# Revit family: Shower-Shower_Trim-KOHLER-Pitch-K-T49990
name_source: partatom
category: Plumbing Fixtures
units: mm (PartAtom-declared; Revit-internal decimal feet)

## family parameters
Cut with Voids When Loaded = No
Host = Face
OmniClass Number = 23.31.17.00
OmniClass Title = Showers
Part Type = Normal
Room Calculation Point = No
Round Connector Dimension = Use Diameter
Shared = No

## types (8) — shared parameters
ADA Compliant = No
Assembly Code = D2010700
CW Connection = No
Cold Water Inlet = Cold Water Inlet
Date Modified = 09/12/2023
Default Elevation = 42"
Drain Included = No
HW Connection = Yes
Handle Clearance = 3 3/8"
Height = 6 3/8"
Hot Water Inlet = Hot Water Inlet
Length = 5 7/8"
Manufacturer = Kohler Co.
Master Format 2014 = 22 42 23
Master Format 2014 Name = Residential Showers
Material = Premium Metal Construction
Panel Thickness = 0"
Pressure = 80.00 psi
Product Documentation Link = https://www.us.kohler.com
Product Name = Pitch
Product Page URL = http://www.us.kohler.com
Tempered Water Inlet = Tempered Water Inlet
URL = https://www.us.kohler.com
Vent Connection = No
Waste Connection = No
Waste Water Outlet = Waste Water Outlet
WaterSense Certified = No
Width = 6 3/8"

## per-type parameters (varying)
| type | Description | Finish | Flow Rate | Model | Type |
| 1.75 GPM, 2MB-Vibrant Brushed Moderne Brass | RT Shower Trim With Diverter, 1.75 GPM | Kohler-Metal-2MB-Vibrant_Brushed_Moderne_Brass | 2 GPM | K-T49990-4G-2MB | 1 |
| 1.75 GPM, BL-Matte Black | RT Shower Trim With Diverter, 1.75 GPM | Kohler-Metal-BL-Matte_Black | 2 GPM | K-T49990-4G-BL | 2 |
| 1.75 GPM, BN-Vibrant Brushed Nickel | RT Shower Trim With Diverter, 1.75 GPM | Kohler-Metal-BN-Vibrant_Brushed_Nickel | 2 GPM | K-T49990-4G-BN | 3 |
| 1.75 GPM, CP-Polished Chrome | RT Shower Trim With Diverter, 1.75 GPM | Kohler-Metal-CP-Polished_Chrome | 2 GPM | K-T49990-4G-CP | 4 |
| 2.5 GPM, 2MB-Vibrant Brushed Moderne Brass | RT Shower Trim With Diverter, 2.5 GPM | Kohler-Metal-2MB-Vibrant_Brushed_Moderne_Brass | 3 GPM | K-T49990-4Y-2MB | 5 |
| 2.5 GPM, BL-Matte Black | RT Shower Trim With Diverter, 2.5 GPM | Kohler-Metal-BL-Matte_Black | 3 GPM | K-T49990-4Y-BL | 6 |
| 2.5 GPM, BN-Vibrant Brushed Nickel | RT Shower Trim With Diverter, 2.5 GPM | Kohler-Metal-BN-Vibrant_Brushed_Nickel | 3 GPM | K-T49990-4Y-BN | 7 |
| 2.5 GPM, CP-Polished Chrome | RT Shower Trim With Diverter, 2.5 GPM | Kohler-Metal-CP-Polished_Chrome | 3 GPM | K-T49990-4Y-CP | 8 |

## geometry (parser evidence)
native form markers: Sweep x9
no freeform markers — native parametric forms only
